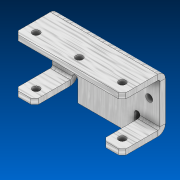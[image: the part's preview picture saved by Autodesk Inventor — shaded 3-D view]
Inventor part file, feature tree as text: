
AUTODESK INVENTOR PART (.ipt)
format: ipt  version: 2022.2 (Build 262287000, 287)  size: 181,248 bytes
history: native  units: in
note: dims shown in document units (in); Inventor stores cm internally (conversion verified against a paired STEP export)
features: extrude x1, sketch x1, chamfer x1
ambient origin geometry x8: Origin, YZ Plane, XZ Plane, XY Plane, X Axis, Y Axis, Z Axis, Center Point
bodies: Solid1 (feature_tree)
feature tree (3):
  extrude  "Extrusion1"  TaperAngle=0.0deg  [1 undecoded]
  sketch  "Sketch1"  dims[d0=1.0in d1=0.0in d2=0.0in]
  chamfer  "Chamfer1"  [1 undecoded]
note: 2 required parameter values undecoded (feature->parameter linkage not recoverable at this tier; creation-order binding heuristic only, values carry confidence <= 0.55)
